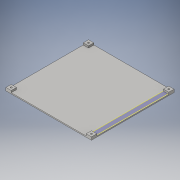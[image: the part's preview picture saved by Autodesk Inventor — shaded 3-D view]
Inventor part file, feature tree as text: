
AUTODESK INVENTOR PART (.ipt)
format: ipt  version: 2016 SP2 (Build 200236200, 236)  size: 163,840 bytes
history: native  units: mm
features: extrude x4, sketch x4, reference x2, plane x1, projected_geometry x1
ambient origin geometry x8: Origin, YZ Plane, XZ Plane, XY Plane, X Axis, Y Axis, Z Axis, Center Point
bodies: Volumenkörper1 (feature_tree)
feature tree (12):
  plane  "Arbeitsebene1"
  extrude  "Extrusion1"  Depth=3.5mm TaperAngle=0.0deg
  extrude  "Extrusion2"  Depth=3.1mm TaperAngle=0.0deg
  extrude  "Extrusion3"  Depth=5.7mm
  extrude  "Extrusion4"  Depth=5.7mm
  sketch  "Skizze1"  dims[d0=2.0mm d1=0.0mm d10=3.5mm d11=0.0mm]
  reference  "Referenz1"
  reference  "Referenz2"
  sketch  "Skizze2"  dims[d12=15.5mm d13=0.0mm d18=3.1mm d19=0.0mm]
  sketch  "Skizze3"  dims[d20=5.7mm d21=5.7mm]
  sketch  "Skizze4"  dims[d22=5.7mm d23=5.7mm d24=0.1mm d25=0.1mm]
  projected_geometry  "Projizierte Kontur1"
